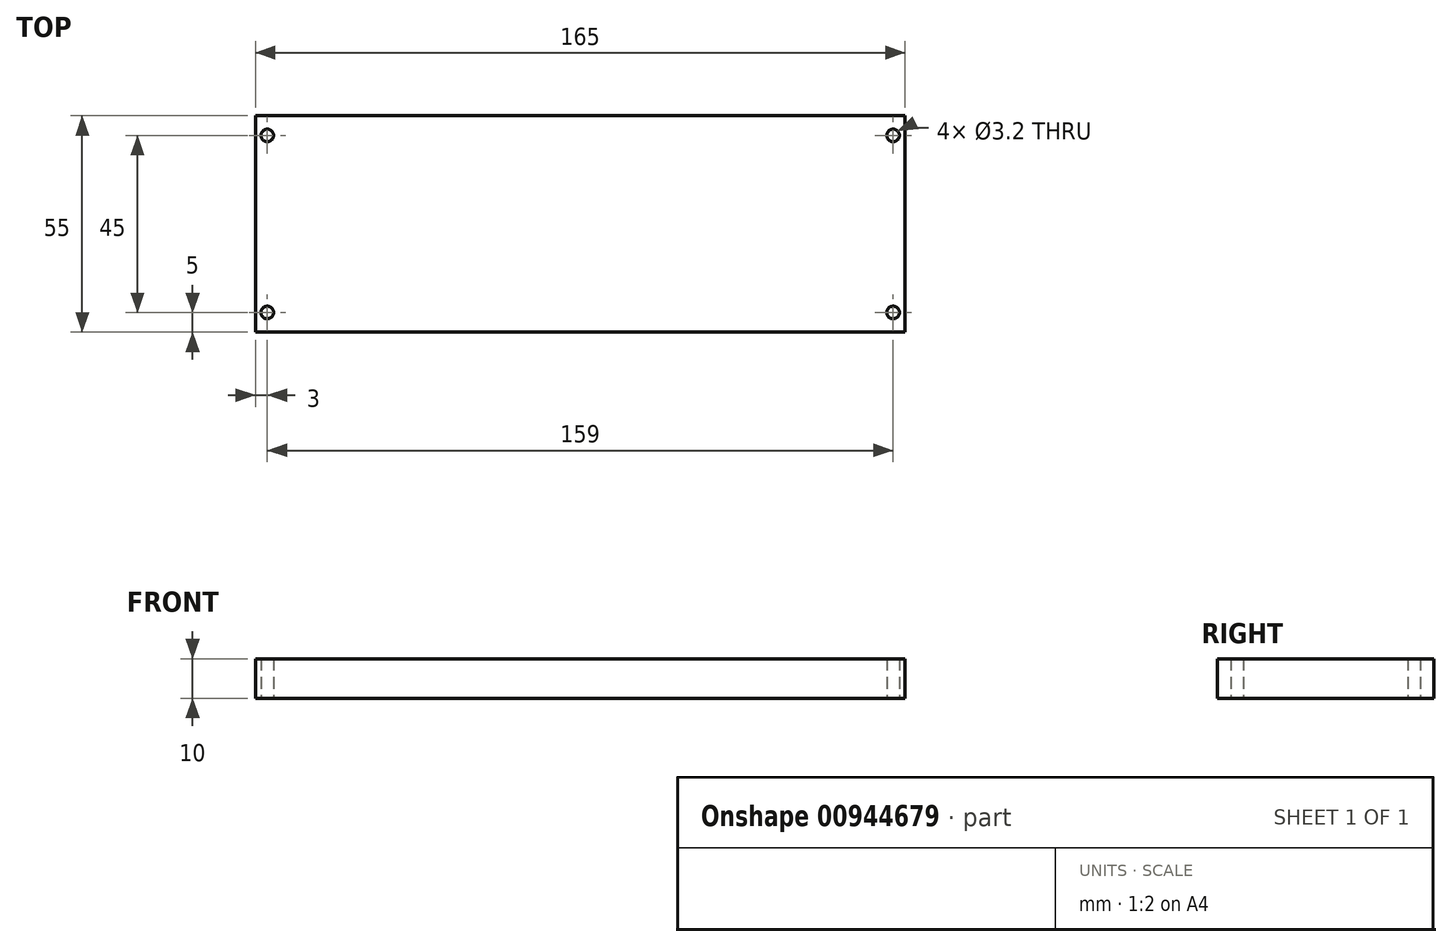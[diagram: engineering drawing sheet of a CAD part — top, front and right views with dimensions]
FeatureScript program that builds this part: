
annotation { "Feature Type Name" : "Feature", "Feature Type Description" : "" }
export const myFeature = defineFeature(function(context is Context, id is Id, definition is map)
    precondition{}
    {
        {
            var Q0;
            Q0=qCreatedBy(makeId("Top.planeOp"),FACE);
            var sketch = newSketch(context, id + "F0", { "sketchPlane" : qUnion([Q0])});
            skLineSegment(sketch, "E0.bottom", {"start": v(82.5, -27.5) * mm, "end": v(-82.5, -27.5) * mm});
            skLineSegment(sketch, "E0.top", {"start": v(82.5, 27.5) * mm, "end": v(-82.5, 27.5) * mm});
            skLineSegment(sketch, "E0.left", {"start": v(82.5, -27.5) * mm, "end": v(82.5, 27.5) * mm});
            skLineSegment(sketch, "E0.right", {"start": v(-82.5, -27.5) * mm, "end": v(-82.5, 27.5) * mm});
            skPoint(sketch, "E0.middle", {"position": v(0, 0) * mm});
            skCircle(sketch, "E1", {"center": v(-79.5, 22.5) * mm, "radius": 1.6 * mm});
            skCircle(sketch, "E2.0.1.0", {"center": v(-79.5, -22.5) * mm, "radius": 1.6 * mm});
            skCircle(sketch, "E2.1.0.0", {"center": v(79.5, 22.5) * mm, "radius": 1.6 * mm});
            skCircle(sketch, "E2.1.1.0", {"center": v(79.5, -22.5) * mm, "radius": 1.6 * mm});
            skLineSegment(sketch, "E2.direction1", {"start": v(-79.5, 22.5) * mm, "end": v(79.5, 22.5) * mm, "construction": true});
            skLineSegment(sketch, "E2.direction2", {"start": v(-79.5, 22.5) * mm, "end": v(-79.5, -22.5) * mm, "construction": true});
            skSolve(sketch);
        }
        {
            var Q0;
            Q0 = qSketchRegion(id + "F0", true);
            extrude(context, id + "F1", {"entities" : qUnion([Q0]), "depth" : 10 * mm, "offsetDistance" : 25 * mm});
        }
    });
